# Revit family: 306_H5_B
name_source: partatom
category: Pipe Accessories
units: mm (PartAtom-declared; Revit-internal decimal feet)

## family parameters
Always vertical = Yes
Cut with Voids When Loaded = No
Part Type = Valve - Breaks Into
Round Connector Dimension = Use Diameter
Shared = No
Work Plane-Based = No

## types (10) — shared parameters
CAT0 = Yes
Description = Globe valve, 3-way, External thread
H10 = 10 mm  [stored 0.0328084 ft]
H22 = 2 mm  [stored 0.00656168 ft]
L2D_Min = 3048 mm
Manufacturer = Belimo
QmdConnectorList = 301;D;302;D;303;D
magiPartTypeId = 306
magiProductFamilyId = H5*B
zero-valued in all types: MC_Default_elevation

## per-type parameters (varying)
- H511B: B=55 mm; B20=19 mm; B4=14 mm  [stored 0.0459318 ft]; B42=16 mm; BH3=34 mm; D=15 mm; G=30 mm  [stored 0.0984252 ft]; G12=42 mm; G48=14 mm  [stored 0.0459318 ft]; G5=15 mm  [stored 0.0492126 ft]; G7=21 mm  [stored 0.0688976 ft]; G8=24 mm  [stored 0.0787402 ft]; H=46 mm; H3=15 mm  [stored 0.0492126 ft]; H3__ve=-15 mm  [stored -0.0492126 ft]; HH3=31 mm; HX=37 mm; HX__ve=-37 mm; L2=25 mm  [stored 0.082021 ft]; L2D=50 mm; LT10=8 mm  [stored 0.0262467 ft]; LT10__ve=-8 mm  [stored -0.0262467 ft]; LT2=40 mm; LT45=64 mm; W2D=15 mm  [stored 0.0492126 ft]
- H550B: B=65 mm; B20=22 mm; B4=16 mm; B42=18 mm; BH3=43 mm; D=50 mm; G=60 mm; G12=84 mm; G48=29 mm; G5=30 mm  [stored 0.0984252 ft]; G7=42 mm; G8=48 mm; H=65 mm; H3=22 mm; H3__ve=-22 mm; HH3=43 mm; HX=44 mm; HX__ve=-44 mm; L2=60 mm; L2D=120 mm; LT10=15 mm  [stored 0.0492126 ft]; LT10__ve=-15 mm  [stored -0.0492126 ft]; LT2=75 mm; LT45=120 mm; W2D=50 mm
- H540B: B=60 mm; B20=20 mm  [stored 0.0656168 ft]; B4=15 mm  [stored 0.0492126 ft]; B42=17 mm  [stored 0.0557743 ft]; BH3=42 mm; D=40 mm; G=55 mm; G12=77 mm; G48=26 mm; G5=28 mm  [stored 0.0918635 ft]; G7=39 mm; G8=44 mm; H=65 mm; H3=22 mm; H3__ve=-22 mm; HH3=43 mm; HX=40 mm; HX__ve=-40 mm  [stored -0.131234 ft]; L2=50 mm; L2D=100 mm; LT10=13 mm  [stored 0.0426509 ft]; LT10__ve=-13 mm  [stored -0.0426509 ft]; LT2=65 mm; LT45=104 mm; W2D=40 mm
- H532B: B=55 mm; B20=19 mm; B4=14 mm  [stored 0.0459318 ft]; B42=16 mm; BH3=37 mm; D=32 mm; G=50 mm; G12=70 mm; G48=24 mm  [stored 0.0787402 ft]; G5=25 mm  [stored 0.082021 ft]; G7=35 mm  [stored 0.114829 ft]; G8=40 mm; H=56 mm; H3=19 mm; H3__ve=-19 mm; HH3=37 mm; HX=37 mm; HX__ve=-37 mm; L2=45 mm; L2D=90 mm; LT10=12 mm  [stored 0.0393701 ft]; LT10__ve=-12 mm  [stored -0.0393701 ft]; LT2=60 mm; LT45=96 mm; W2D=32 mm  [stored 0.104987 ft]
- H525B: B=55 mm; B20=19 mm; B4=14 mm  [stored 0.0459318 ft]; B42=16 mm; BH3=36 mm; D=25 mm; G=40 mm; G12=56 mm; G48=19 mm; G5=20 mm  [stored 0.0656168 ft]; G7=28 mm  [stored 0.0918635 ft]; G8=32 mm  [stored 0.104987 ft]; H=52 mm; H3=17 mm  [stored 0.0557743 ft]; H3__ve=-17 mm; HH3=35 mm  [stored 0.114829 ft]; HX=37 mm; HX__ve=-37 mm; L2=40 mm; L2D=80 mm; LT10=11 mm  [stored 0.0360892 ft]; LT10__ve=-11 mm  [stored -0.0360892 ft]; LT2=55 mm; LT45=88 mm; W2D=25 mm  [stored 0.082021 ft]
- H520B: B=55 mm; B20=19 mm; B4=14 mm  [stored 0.0459318 ft]; B42=16 mm; BH3=34 mm; D=20 mm; G=35 mm  [stored 0.114829 ft]; G12=49 mm; G48=17 mm  [stored 0.0557743 ft]; G5=18 mm; G7=25 mm  [stored 0.082021 ft]; G8=28 mm  [stored 0.0918635 ft]; H=46 mm; H3=15 mm  [stored 0.0492126 ft]; H3__ve=-15 mm  [stored -0.0492126 ft]; HH3=31 mm; HX=37 mm; HX__ve=-37 mm; L2=30 mm  [stored 0.0984252 ft]; L2D=60 mm; LT10=9 mm  [stored 0.0295276 ft]; LT10__ve=-9 mm  [stored -0.0295276 ft]; LT2=45 mm; LT45=72 mm; W2D=20 mm  [stored 0.0656168 ft]
- H515B: B=55 mm; B20=19 mm; B4=14 mm  [stored 0.0459318 ft]; B42=16 mm; BH3=34 mm; D=15 mm; G=30 mm  [stored 0.0984252 ft]; G12=42 mm; G48=14 mm  [stored 0.0459318 ft]; G5=15 mm  [stored 0.0492126 ft]; G7=21 mm  [stored 0.0688976 ft]; G8=24 mm  [stored 0.0787402 ft]; H=46 mm; H3=15 mm  [stored 0.0492126 ft]; H3__ve=-15 mm  [stored -0.0492126 ft]; HH3=31 mm; HX=37 mm; HX__ve=-37 mm; L2=25 mm  [stored 0.082021 ft]; L2D=50 mm; LT10=8 mm  [stored 0.0262467 ft]; LT10__ve=-8 mm  [stored -0.0262467 ft]; LT2=40 mm; LT45=64 mm; W2D=15 mm  [stored 0.0492126 ft]
- H514B: B=55 mm; B20=19 mm; B4=14 mm  [stored 0.0459318 ft]; B42=16 mm; BH3=34 mm; D=15 mm; G=30 mm  [stored 0.0984252 ft]; G12=42 mm; G48=14 mm  [stored 0.0459318 ft]; G5=15 mm  [stored 0.0492126 ft]; G7=21 mm  [stored 0.0688976 ft]; G8=24 mm  [stored 0.0787402 ft]; H=46 mm; H3=15 mm  [stored 0.0492126 ft]; H3__ve=-15 mm  [stored -0.0492126 ft]; HH3=31 mm; HX=37 mm; HX__ve=-37 mm; L2=25 mm  [stored 0.082021 ft]; L2D=50 mm; LT10=8 mm  [stored 0.0262467 ft]; LT10__ve=-8 mm  [stored -0.0262467 ft]; LT2=40 mm; LT45=64 mm; W2D=15 mm  [stored 0.0492126 ft]
- H513B: B=55 mm; B20=19 mm; B4=14 mm  [stored 0.0459318 ft]; B42=16 mm; BH3=34 mm; D=15 mm; G=30 mm  [stored 0.0984252 ft]; G12=42 mm; G48=14 mm  [stored 0.0459318 ft]; G5=15 mm  [stored 0.0492126 ft]; G7=21 mm  [stored 0.0688976 ft]; G8=24 mm  [stored 0.0787402 ft]; H=46 mm; H3=15 mm  [stored 0.0492126 ft]; H3__ve=-15 mm  [stored -0.0492126 ft]; HH3=31 mm; HX=37 mm; HX__ve=-37 mm; L2=25 mm  [stored 0.082021 ft]; L2D=50 mm; LT10=8 mm  [stored 0.0262467 ft]; LT10__ve=-8 mm  [stored -0.0262467 ft]; LT2=40 mm; LT45=64 mm; W2D=15 mm  [stored 0.0492126 ft]
- H512B: B=55 mm; B20=19 mm; B4=14 mm  [stored 0.0459318 ft]; B42=16 mm; BH3=34 mm; D=15 mm; G=30 mm  [stored 0.0984252 ft]; G12=42 mm; G48=14 mm  [stored 0.0459318 ft]; G5=15 mm  [stored 0.0492126 ft]; G7=21 mm  [stored 0.0688976 ft]; G8=24 mm  [stored 0.0787402 ft]; H=46 mm; H3=15 mm  [stored 0.0492126 ft]; H3__ve=-15 mm  [stored -0.0492126 ft]; HH3=31 mm; HX=37 mm; HX__ve=-37 mm; L2=25 mm  [stored 0.082021 ft]; L2D=50 mm; LT10=8 mm  [stored 0.0262467 ft]; LT10__ve=-8 mm  [stored -0.0262467 ft]; LT2=40 mm; LT45=64 mm; W2D=15 mm  [stored 0.0492126 ft]

note: column(s) folded — value = type name in every type: magiProductCode, magiProductId

note: [stored X ft] marks values corroborated as IEEE doubles in the binary element streams (Revit-internal decimal feet)

## geometry (parser evidence)
native form markers: Sweep x1
no freeform markers — native parametric forms only
